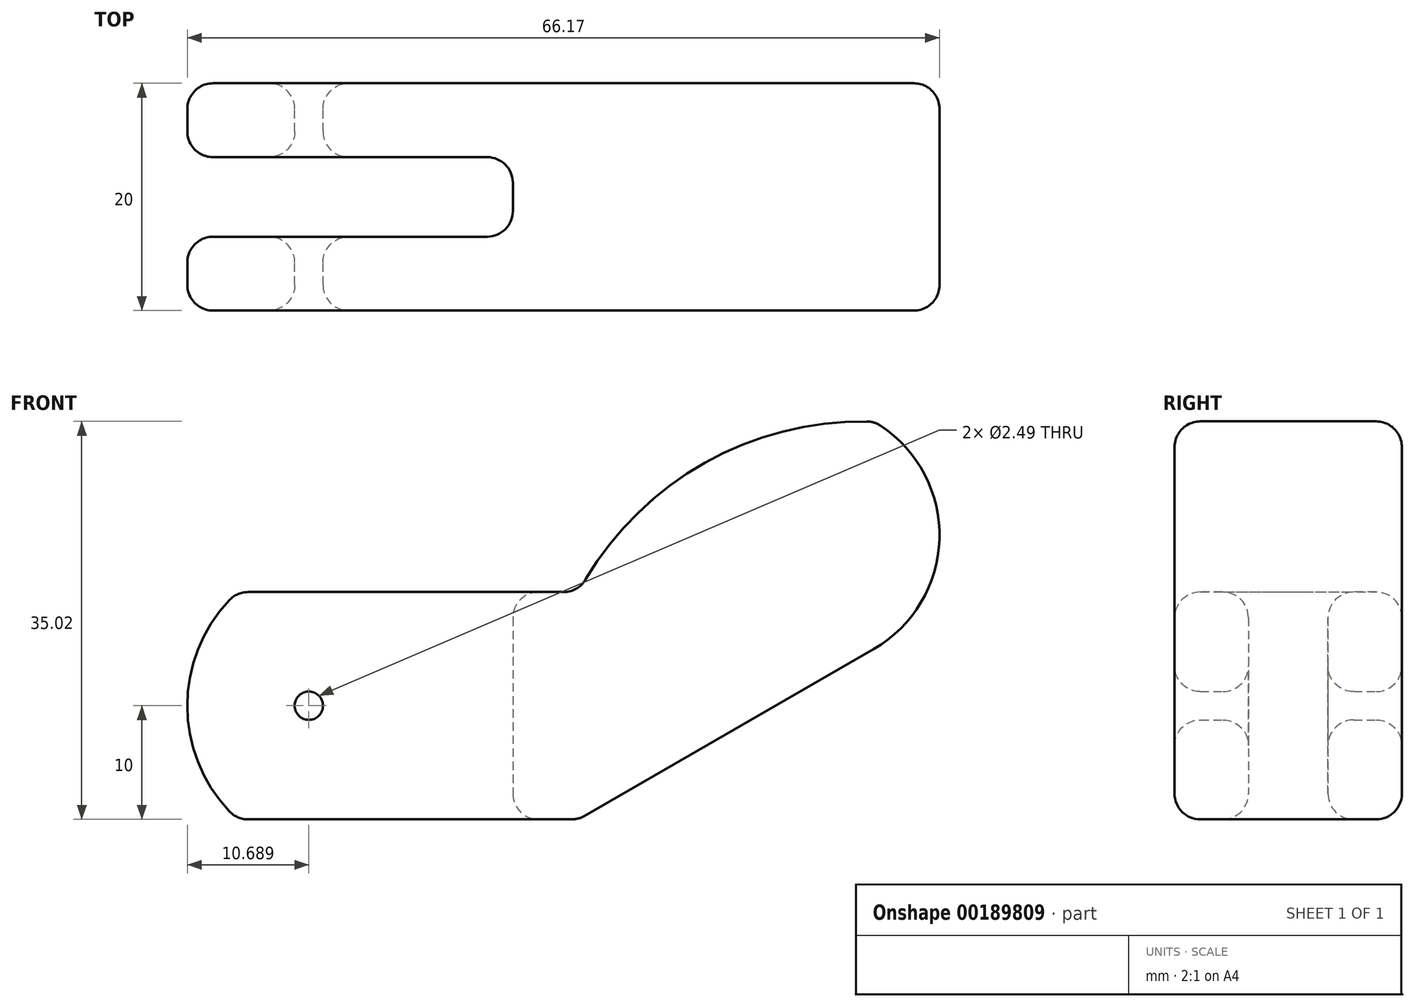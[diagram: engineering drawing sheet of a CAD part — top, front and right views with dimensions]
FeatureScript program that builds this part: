
annotation { "Feature Type Name" : "Feature", "Feature Type Description" : "" }
export const myFeature = defineFeature(function(context is Context, id is Id, definition is map)
    precondition{}
    {
        {
            var Q0;
            Q0=qCreatedBy(makeId("Front.planeOp"),FACE);
            var sketch = newSketch(context, id + "F0", { "sketchPlane" : qUnion([Q0])});
            skLineSegment(sketch, "E0.right", {"start": v(30, 0) * mm, "end": v(30, 20) * mm});
            skLineSegment(sketch, "E1", {"start": v(10.1, 0) * mm, "end": v(10.1, 20) * mm, "construction": true});
            skLineSegment(sketch, "E2", {"start": v(30, 10) * mm, "end": v(0, 10) * mm, "construction": true});
            skLineSegment(sketch, "E3", {"start": v(30, 20) * mm, "end": v(55.98, 35) * mm});
            skLineSegment(sketch, "E4", {"start": v(55.98, 35) * mm, "end": v(55.98, 15) * mm});
            skLineSegment(sketch, "E5", {"start": v(30, 0) * mm, "end": v(55.98, 15) * mm});
            skArc(sketch, "E6", {"start": v(55.98, 35) * mm, "mid": v(40.84, 31.22) * mm, "end": v(30, 20) * mm});
            skArc(sketch, "E7", {"start": v(55.98, 15) * mm, "mid": v(61.75, 25) * mm, "end": v(55.98, 35) * mm});
            skLineSegment(sketch, "E8", {"start": v(30, 20) * mm, "end": v(30, 0) * mm, "construction": true});
            skLineSegment(sketch, "E9", {"start": v(0, 10) * mm, "end": v(6.27, 10) * mm, "construction": true});
            skCircle(sketch, "E10", {"center": v(6.27, 10) * mm, "radius": 1.24 * mm});
            skPoint(sketch, "E11.orphan", {"position": v(0, 20) * mm});
            skArc(sketch, "E12", {"start": v(0, 20) * mm, "mid": v(-4.42, 10) * mm, "end": v(0, 0) * mm});
            skLineSegment(sketch, "E13.trimOffspring", {"start": v(7.51, 10) * mm, "end": v(5.02, 10) * mm, "construction": true});
            skPoint(sketch, "E14.start.orphan", {"position": v(10.1, 10) * mm});
            skLineSegment(sketch, "E15", {"start": v(0, 20) * mm, "end": v(30, 20) * mm});
            skLineSegment(sketch, "E16", {"start": v(0, 0) * mm, "end": v(30, 0) * mm});
            skSolve(sketch);
        }
        {
            var Q0;
            Q0 = qSketchRegion(id + "F0", true);
            extrude(context, id + "F1", {"entities" : qUnion([Q0]), "depth" : 20 * mm});
        }
        {
            var Q0;
            Q0=makeQuery(id+"F1.opExtrude","SWEPT_FACE",FACE,{"disambiguationData":[OSD([sQuery(id+"F0.wireOp",EDGE,"E16")])]});
            var sketch = newSketch(context, id + "F2", { "sketchPlane" : qUnion([Q0])});
            skPoint(sketch, "E17.end.orphan", {"position": v(6.5, 0) * mm});
            skLineSegment(sketch, "E18.top", {"start": v(14.55, 13.5) * mm, "end": v(-6.26, 13.5) * mm});
            skLineSegment(sketch, "E19.top", {"start": v(-6.24, 6.5) * mm, "end": v(24.22, 6.5) * mm});
            skLineSegment(sketch, "E20.trimOffspring", {"start": v(-6.24, 10) * mm, "end": v(-6.26, 10) * mm});
            skLineSegment(sketch, "E21.trimOffspring", {"start": v(14.55, 10) * mm, "end": v(14.56, 10) * mm});
            skPoint(sketch, "E18.bottom.end.orphan", {"position": v(5.05, 10) * mm});
            skLineSegment(sketch, "E22", {"start": v(-5.55, -518.89) * mm, "end": v(-5.55, -516.94) * mm, "construction": true});
            skLineSegment(sketch, "E23", {"start": v(-5.55, -497.05) * mm, "end": v(14.55, -497.05) * mm, "construction": true});
            skLineSegment(sketch, "E24.bottom", {"start": v(-6.26, 13.5) * mm, "end": v(14.56, 13.5) * mm});
            skLineSegment(sketch, "E24.top", {"start": v(-6.26, 6.5) * mm, "end": v(24.22, 6.5) * mm});
            skLineSegment(sketch, "E25.bottom", {"start": v(-6.26, 13.5) * mm, "end": v(24.22, 13.5) * mm});
            skLineSegment(sketch, "E25.left", {"start": v(-6.26, 13.5) * mm, "end": v(-6.26, 6.5) * mm});
            skLineSegment(sketch, "E25.right", {"start": v(24.22, 13.5) * mm, "end": v(24.22, 6.5) * mm});
            skSolve(sketch);
        }
        {
            var Q0;
            Q0 = qSketchRegion(id + "F2", true);
            extrude(context, id + "F3", {"entities" : qUnion([Q0]), "operationType" : NewBodyOperationType.REMOVE, "oppositeDirection" : true, "depth" : 20 * mm});
        }
        {
            var Q0;
            Q0=makeQuery(id+"F1.opExtrude","CAP_FACE",FACE,{"disambiguationData":[OSD([sQuery(id+"F0.wireOp",EDGE,"E5"),sQuery(id+"F0.wireOp",EDGE,"E6"),sQuery(id+"F0.wireOp",EDGE,"E7"),sQuery(id+"F0.wireOp",EDGE,"E10"),sQuery(id+"F0.wireOp",EDGE,"E12"),sQuery(id+"F0.wireOp",EDGE,"E15"),sQuery(id+"F0.wireOp",EDGE,"E16")])],"isStart":true});
            var Q1;
            Q1=makeQuery(id+"F1.opExtrude","SWEPT_FACE",FACE,{"disambiguationData":[OSD([sQuery(id+"F0.wireOp",EDGE,"E15")])]});
            var Q2;
            Q2=makeQuery(id+"F1.opExtrude","SWEPT_FACE",FACE,{"disambiguationData":[OSD([sQuery(id+"F0.wireOp",EDGE,"E6")])]});
            var Q3;
            Q3=makeQuery(id+"F1.opExtrude","SWEPT_FACE",FACE,{"disambiguationData":[OSD([sQuery(id+"F0.wireOp",EDGE,"E7")])]});
            var Q4;
            Q4=makeQuery(id+"F1.opExtrude","SWEPT_FACE",FACE,{"disambiguationData":[OSD([sQuery(id+"F0.wireOp",EDGE,"E5")])]});
            var Q5;
            Q5=makeQuery(id+"F1.opExtrude","SWEPT_FACE",FACE,{"disambiguationData":[OSD([sQuery(id+"F0.wireOp",EDGE,"E16")])]});
            var Q6;
            Q6=makeQuery(id+"F1.opExtrude","CAP_FACE",FACE,{"disambiguationData":[OSD([sQuery(id+"F0.wireOp",EDGE,"E5"),sQuery(id+"F0.wireOp",EDGE,"E6"),sQuery(id+"F0.wireOp",EDGE,"E7"),sQuery(id+"F0.wireOp",EDGE,"E10"),sQuery(id+"F0.wireOp",EDGE,"E12"),sQuery(id+"F0.wireOp",EDGE,"E15"),sQuery(id+"F0.wireOp",EDGE,"E16")])],"isStart":false});
            var Q7;
            Q7=makeQuery(id+"F3.boolean.opBoolean","COPY",FACE,{"derivedFrom":makeQuery(id+"F3.opExtrude","SWEPT_FACE",FACE,{"disambiguationData":[OSD([sQuery(id+"F2.wireOp",EDGE,"E25.right")])]})});
            var Q8;
            Q8=makeQuery(id+"F3.boolean.opBoolean","COPY",FACE,{"derivedFrom":makeQuery(id+"F3.opExtrude","SWEPT_FACE",FACE,{"disambiguationData":[OSD([sQuery(id+"F2.wireOp",EDGE,"E24.top")])]})});
            var Q9;
            Q9=makeQuery(id+"F3.boolean.opBoolean","COPY",FACE,{"derivedFrom":makeQuery(id+"F3.opExtrude","SWEPT_FACE",FACE,{"disambiguationData":[OSD([sQuery(id+"F2.wireOp",EDGE,"E25.bottom")])]})});
            fillet(context, id + "F4", {"entities" : qUnion([Q0, Q1, Q2, Q3, Q4, Q5, Q6, Q7, Q8, Q9]), "radius" : 2.26 * mm, "tangentPropagation" : true, "allowEdgeOverflow" : false});
        }
    });
